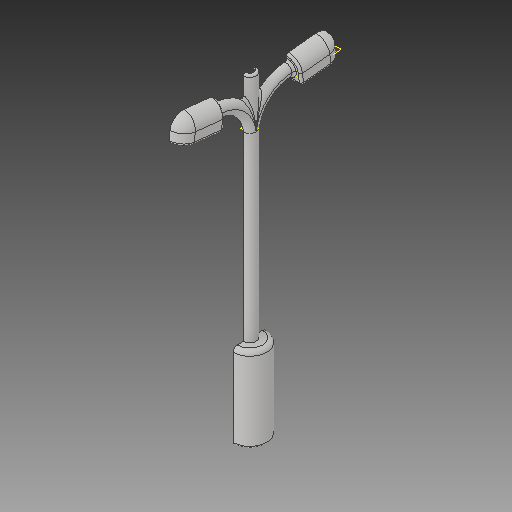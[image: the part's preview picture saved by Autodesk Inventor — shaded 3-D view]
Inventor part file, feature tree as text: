
AUTODESK INVENTOR PART (.ipt)
format: ipt  version: 2018 (Build 220112000, 112)  size: 489,984 bytes
history: native  units: in
note: dims shown in document units (in); Inventor stores cm internally (conversion verified against a paired STEP export)
features: sketch x11, other x3, plane x1
ambient origin geometry x8: Origin, YZ Plane, XZ Plane, XY Plane, X Axis, Y Axis, Z Axis, Center Point
bodies: Solid1 (feature_tree)
feature tree (15):
  other  "lampa_dual.ipt"
  other  "Solid1::lampa_dual.ipt"
  other  "TaggingFeature1"
  sketch  "Sketch1"  dims[d0=0.3937in]
  sketch  "Sketch6"
  sketch  "Sketch8"
  sketch  "Sketch9"
  sketch  "Sketch10"
  sketch  "Sketch11"
  sketch  "Sketch12"
  sketch  "Sketch13"
  sketch  "Sketch14"
  sketch  "Sketch15"
  sketch  "Sketch16"
  plane  "Work Plane1"
